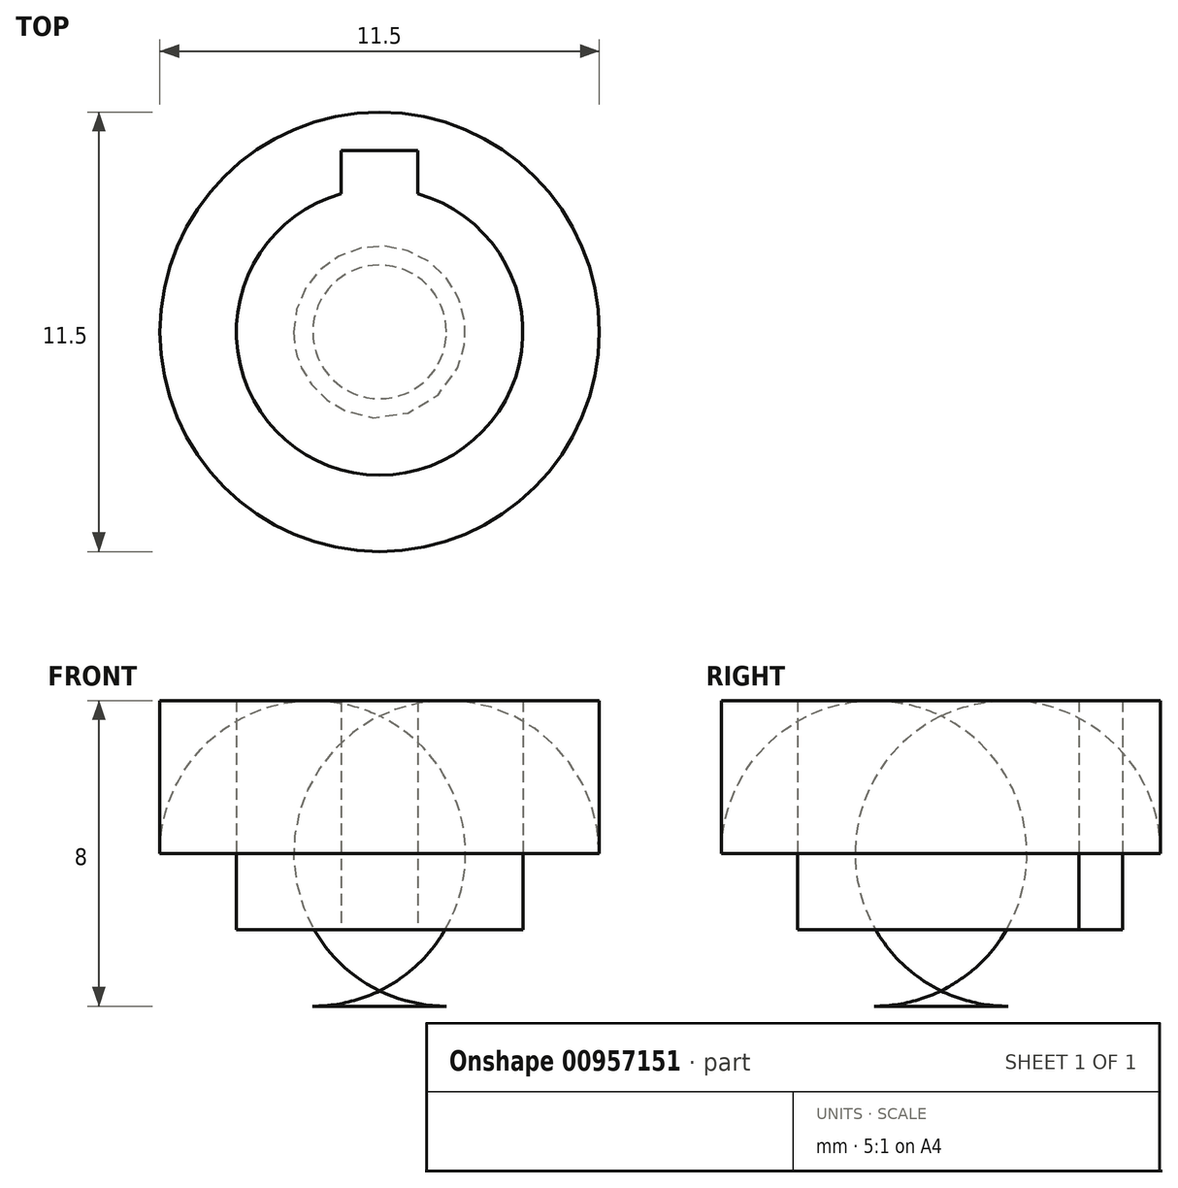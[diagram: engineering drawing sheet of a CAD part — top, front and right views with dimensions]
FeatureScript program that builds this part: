
annotation { "Feature Type Name" : "Feature", "Feature Type Description" : "" }
export const myFeature = defineFeature(function(context is Context, id is Id, definition is map)
    precondition{}
    {
        {
            var Q0;
            Q0=qCreatedBy(makeId("Top.planeOp"),FACE);
            var sketch = newSketch(context, id + "F0", { "sketchPlane" : qUnion([Q0])});
            skCircle(sketch, "E0", {"center": v(0, 0) * mm, "radius": 3.75 * mm});
            skCircle(sketch, "E1", {"center": v(0, 0) * mm, "radius": 5.75 * mm});
            skLineSegment(sketch, "E2.bottom", {"start": v(-1, 4.75) * mm, "end": v(1, 4.75) * mm});
            skLineSegment(sketch, "E2.top", {"start": v(-1, 2.75) * mm, "end": v(1, 2.75) * mm});
            skLineSegment(sketch, "E2.left", {"start": v(-1, 4.75) * mm, "end": v(-1, 2.75) * mm});
            skLineSegment(sketch, "E2.right", {"start": v(1, 4.75) * mm, "end": v(1, 2.75) * mm});
            skPoint(sketch, "E2.middle", {"position": v(0, 3.75) * mm});
            skSolve(sketch);
        }
        {
            var Q0;
            Q0=makeQuery(id+"F0.imprint","IMPRINT",FACE,{"disambiguationData":[TD([[makeQuery(id+"F0.imprint","IMPRINT",EDGE,{"derivedFrom":sQuery(id+"F0.wireOp",EDGE,"E1")}),1.0]])]});
            extrude(context, id + "F1", {"entities" : qUnion([Q0]), "depth" : 8 * mm, "offsetDistance" : 25 * mm});
        }
        {
            var Q0;
            {var subQ5=sQuery(id+"F0.wireOp",EDGE,"E2.bottom");Q0=makeQuery(id+"F0.imprint","IMPRINT",FACE,{"disambiguationData":[TD([[makeQuery(id+"F0.imprint","IMPRINT",EDGE,{"derivedFrom":subQ5}),-1.0]])]});}
            var Q1;
            {var subQ5=sQuery(id+"F0.wireOp",EDGE,"E2.top");Q1=makeQuery(id+"F0.imprint","IMPRINT",FACE,{"disambiguationData":[TD([[makeQuery(id+"F0.imprint","IMPRINT",EDGE,{"derivedFrom":subQ5}),1.0]])]});}
            var Q2;
            {var subQ5=sQuery(id+"F0.wireOp",EDGE,"E2.top");Q2=makeQuery(id+"F0.imprint","IMPRINT",FACE,{"disambiguationData":[TD([[makeQuery(id+"F0.imprint","IMPRINT",EDGE,{"derivedFrom":subQ5}),-1.0]])]});}
            extrude(context, id + "F2", {"entities" : qUnion([Q0, Q1, Q2]), "operationType" : NewBodyOperationType.ADD, "depth" : 2 * mm, "offsetDistance" : 25 * mm});
        }
        {
            var Q0;
            Q0=makeQuery(id+"F1.opExtrude","CAP_EDGE",EDGE,{"disambiguationData":[OSD([sQuery(id+"F0.wireOp",EDGE,"E1")])],"isStart":true});
            fillet(context, id + "F3", {"entities" : qUnion([Q0]), "radius" : 4 * mm, "tangentPropagation" : true, "allowEdgeOverflow" : false});
        }
    });
